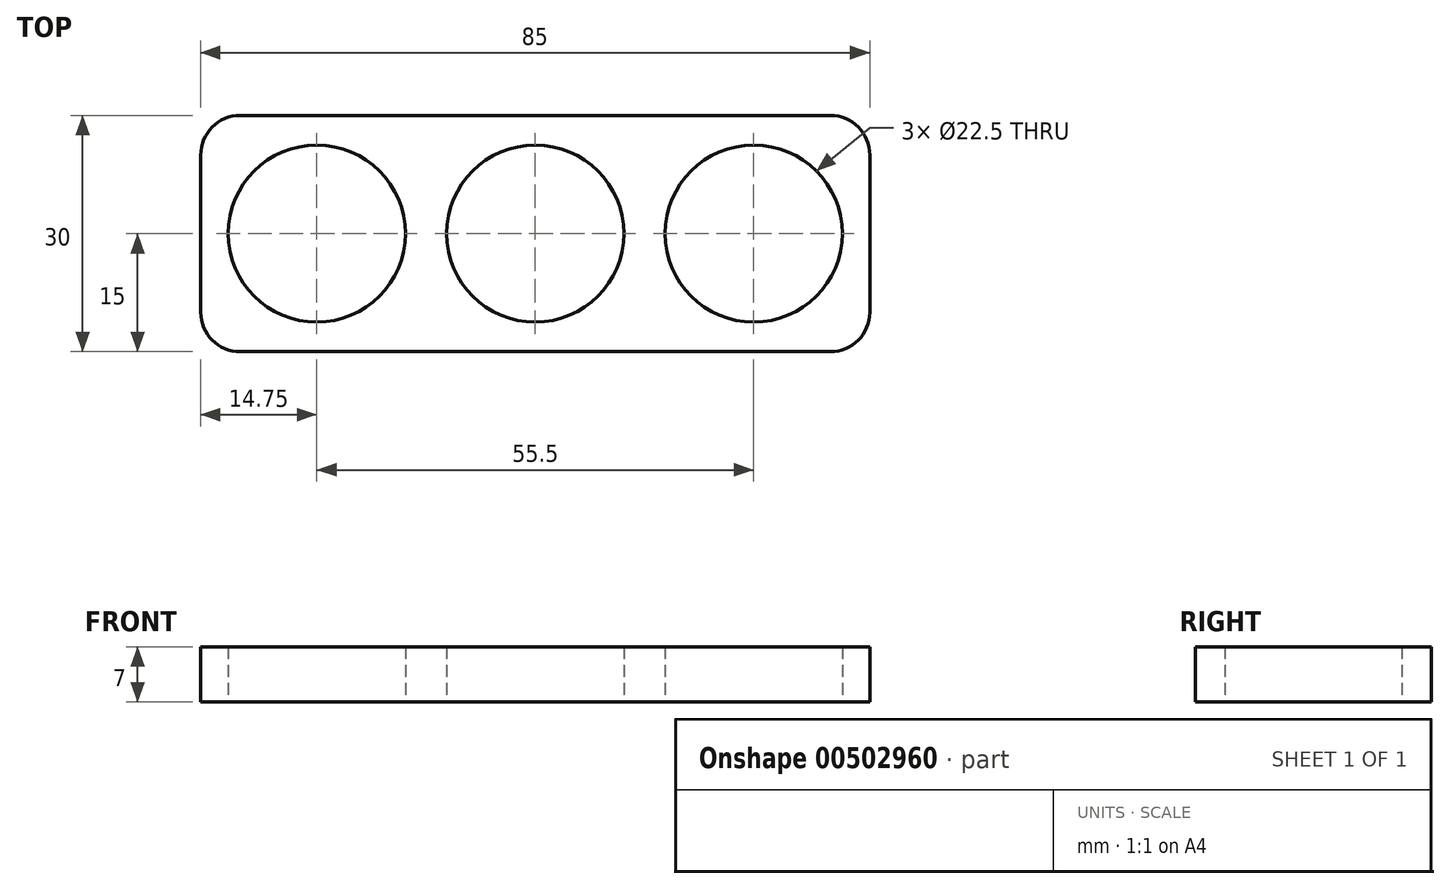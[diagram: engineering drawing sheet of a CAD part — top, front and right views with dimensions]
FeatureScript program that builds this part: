
annotation { "Feature Type Name" : "Feature", "Feature Type Description" : "" }
export const myFeature = defineFeature(function(context is Context, id is Id, definition is map)
    precondition{}
    {
        {
            var Q0;
            Q0=qCreatedBy(makeId("Top.planeOp"),FACE);
            var sketch = newSketch(context, id + "F0", { "sketchPlane" : qUnion([Q0])});
            skLineSegment(sketch, "E0.bottom", {"start": v(37.5, 15) * mm, "end": v(-37.5, 15) * mm});
            skLineSegment(sketch, "E0.top", {"start": v(37.5, -15) * mm, "end": v(-37.5, -15) * mm});
            skLineSegment(sketch, "E0.left", {"start": v(42.5, 10) * mm, "end": v(42.5, -10) * mm});
            skLineSegment(sketch, "E0.right", {"start": v(-42.5, 10) * mm, "end": v(-42.5, -10) * mm});
            skPoint(sketch, "E0.middle", {"position": v(0, 0) * mm});
            skPoint(sketch, "E1.visualSharp", {"position": v(-42.5, 15) * mm});
            skArc(sketch, "E1.filletArc", {"start": v(-37.5, 15) * mm, "mid": v(-41.04, 13.54) * mm, "end": v(-42.5, 10) * mm});
            skPoint(sketch, "E2.visualSharp", {"position": v(42.5, 15) * mm});
            skArc(sketch, "E2.filletArc", {"start": v(42.5, 10) * mm, "mid": v(41.04, 13.54) * mm, "end": v(37.5, 15) * mm});
            skPoint(sketch, "E3.visualSharp", {"position": v(42.5, -15) * mm});
            skArc(sketch, "E3.filletArc", {"start": v(37.5, -15) * mm, "mid": v(41.04, -13.54) * mm, "end": v(42.5, -10) * mm});
            skPoint(sketch, "E4.visualSharp", {"position": v(-42.5, -15) * mm});
            skArc(sketch, "E4.filletArc", {"start": v(-42.5, -10) * mm, "mid": v(-41.04, -13.54) * mm, "end": v(-37.5, -15) * mm});
            skCircle(sketch, "E5", {"center": v(-27.75, 0) * mm, "radius": 11.25 * mm});
            skCircle(sketch, "E6", {"center": v(27.75, 0) * mm, "radius": 11.25 * mm});
            skCircle(sketch, "E7", {"center": v(0, 0) * mm, "radius": 11.25 * mm});
            skSolve(sketch);
        }
        {
            var Q0;
            Q0=makeQuery(id+"F0.imprint","IMPRINT",FACE,{"disambiguationData":[TD([[makeQuery(id+"F0.imprint","IMPRINT",EDGE,{"derivedFrom":sQuery(id+"F0.wireOp",EDGE,"E0.bottom")}),1.0]])]});
            extrude(context, id + "F1", {"entities" : qUnion([Q0]), "depth" : 7 * mm});
        }
    });
